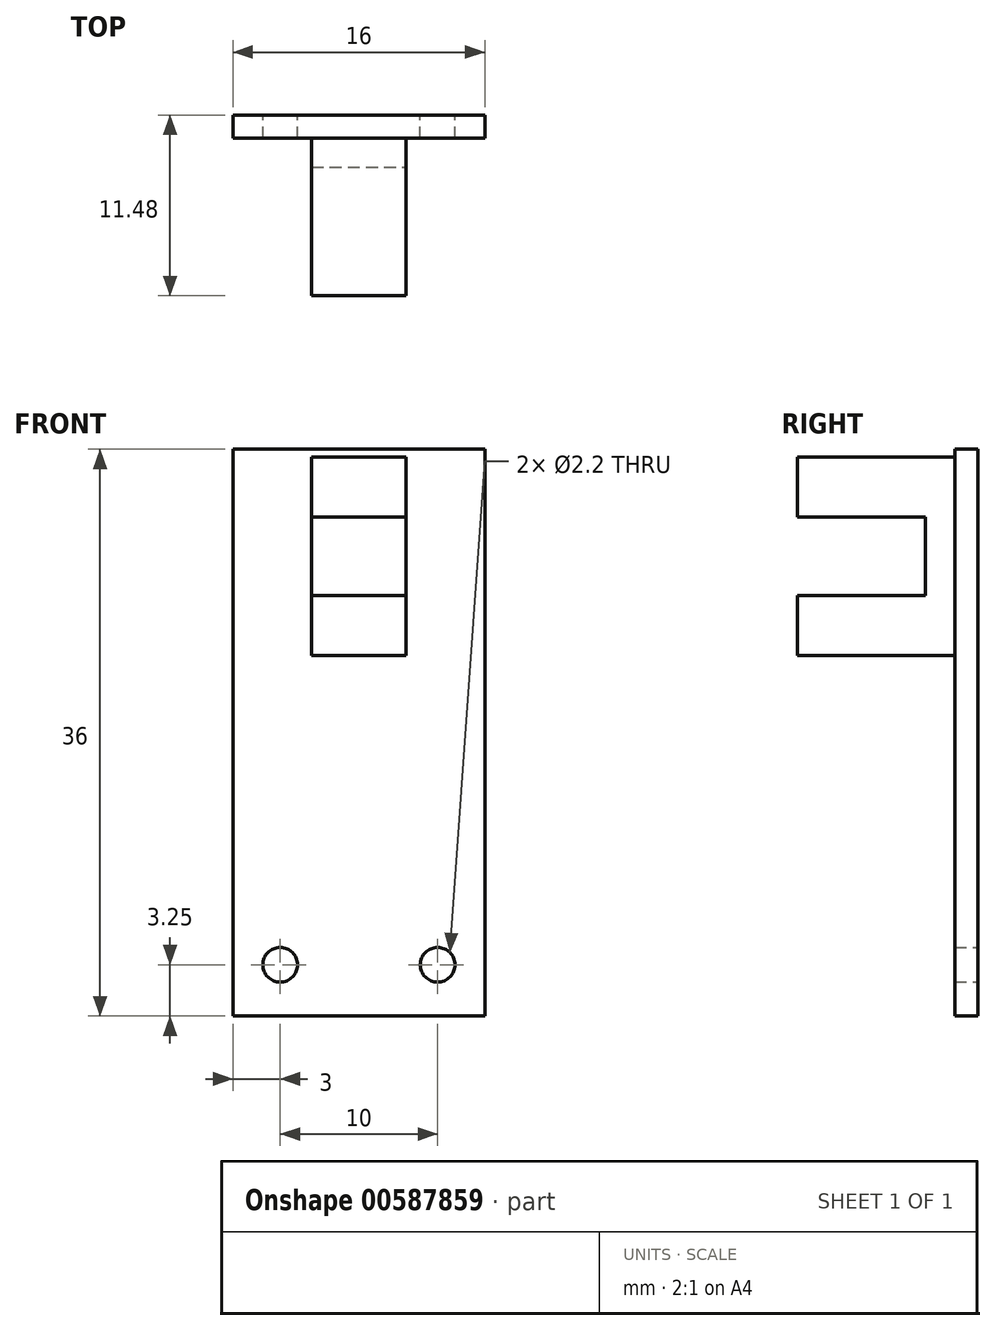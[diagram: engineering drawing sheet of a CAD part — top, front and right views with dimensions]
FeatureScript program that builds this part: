
annotation { "Feature Type Name" : "Feature", "Feature Type Description" : "" }
export const myFeature = defineFeature(function(context is Context, id is Id, definition is map)
    precondition{}
    {
        {
            var Q0;
            Q0=qCreatedBy(makeId("Front.planeOp"),FACE);
            var sketch = newSketch(context, id + "F0", { "sketchPlane" : qUnion([Q0])});
            skLineSegment(sketch, "E0.bottom", {"start": v(0, 0) * mm, "end": v(16, 0) * mm});
            skLineSegment(sketch, "E0.top", {"start": v(0, -36) * mm, "end": v(16, -36) * mm});
            skLineSegment(sketch, "E0.left", {"start": v(0, 0) * mm, "end": v(0, -36) * mm});
            skLineSegment(sketch, "E0.right", {"start": v(16, 0) * mm, "end": v(16, -36) * mm});
            skCircle(sketch, "E1", {"center": v(3, -32.75) * mm, "radius": 1.1 * mm});
            skCircle(sketch, "E2", {"center": v(13, -32.75) * mm, "radius": 1.1 * mm});
            skPoint(sketch, "E3", {"position": v(8, -36) * mm});
            skLineSegment(sketch, "E4", {"start": v(3, -32.75) * mm, "end": v(13, -32.75) * mm, "construction": true});
            skPoint(sketch, "E5", {"position": v(8, -32.75) * mm});
            skSolve(sketch);
        }
        {
            var Q0;
            Q0=makeQuery(id+"F0.imprint","IMPRINT",FACE,{"disambiguationData":[TD([[makeQuery(id+"F0.imprint","IMPRINT",EDGE,{"derivedFrom":sQuery(id+"F0.wireOp",EDGE,"E0.bottom")}),-1.0]])]});
            extrude(context, id + "F1", {"entities" : qUnion([Q0]), "depth" : 1.48 * mm, "offsetDistance" : 25 * mm});
        }
        {
            var Q0;
            Q0=makeQuery(id+"F1.opExtrude","CAP_FACE",FACE,{"disambiguationData":[OSD([sQuery(id+"F0.wireOp",EDGE,"E0.bottom"),sQuery(id+"F0.wireOp",EDGE,"E0.top"),sQuery(id+"F0.wireOp",EDGE,"E0.left"),sQuery(id+"F0.wireOp",EDGE,"E0.right")])],"isStart":false});
            var sketch = newSketch(context, id + "F2", { "sketchPlane" : qUnion([Q0])});
            skSolve(sketch);
        }
        {
            var Q0;
            Q0=makeQuery(id+"F2.imprint","IMPRINT",FACE,{"disambiguationData":[TD([[makeQuery(id+"F2.imprint","IMPRINT",EDGE,{"derivedFrom":makeQuery(id+"F1.opExtrude","CAP_EDGE",EDGE,{"disambiguationData":[OSD([sQuery(id+"F0.wireOp",EDGE,"E0.bottom")])],"isStart":false})}),-1.0]])]});
            var sketch = newSketch(context, id + "F3", { "sketchPlane" : qUnion([Q0])});
            skLineSegment(sketch, "E6.bottom", {"start": v(5, -0.5) * mm, "end": v(11, -0.5) * mm});
            skLineSegment(sketch, "E6.top", {"start": v(5, -13.1) * mm, "end": v(11, -13.1) * mm});
            skLineSegment(sketch, "E6.left", {"start": v(5, -0.5) * mm, "end": v(5, -13.1) * mm});
            skLineSegment(sketch, "E6.right", {"start": v(11, -0.5) * mm, "end": v(11, -13.1) * mm});
            skPoint(sketch, "E7", {"position": v(8, -0.5) * mm});
            skLineSegment(sketch, "E8.0", {"start": v(0, 0) * mm, "end": v(16, 0) * mm, "construction": true});
            skPoint(sketch, "E9", {"position": v(8, 0) * mm});
            skLineSegment(sketch, "E10", {"start": v(5, -4.3) * mm, "end": v(11, -4.3) * mm});
            skLineSegment(sketch, "E11", {"start": v(5, -9.3) * mm, "end": v(11, -9.3) * mm});
            skSolve(sketch);
        }
        {
            var Q0;
            {var subQ0=sQuery(id+"F3.wireOp",EDGE,"E6.top");Q0=makeQuery(id+"F3.imprint","IMPRINT",FACE,{"disambiguationData":[TD([[makeQuery(id+"F3.imprint","IMPRINT",EDGE,{"derivedFrom":subQ0}),1.0]])]});}
            var Q1;
            {var subQ0=sQuery(id+"F3.wireOp",EDGE,"E6.bottom");Q1=makeQuery(id+"F3.imprint","IMPRINT",FACE,{"disambiguationData":[TD([[makeQuery(id+"F3.imprint","IMPRINT",EDGE,{"derivedFrom":subQ0}),-1.0]])]});}
            extrude(context, id + "F4", {"entities" : qUnion([Q0, Q1]), "operationType" : NewBodyOperationType.ADD, "depth" : 10 * mm, "offsetDistance" : 25 * mm});
        }
        {
            var Q0;
            {var subQ0=sQuery(id+"F3.wireOp",EDGE,"E10");Q0=makeQuery(id+"F3.imprint","IMPRINT",FACE,{"disambiguationData":[TD([[makeQuery(id+"F3.imprint","IMPRINT",EDGE,{"derivedFrom":subQ0}),-1.0]])]});}
            extrude(context, id + "F5", {"entities" : qUnion([Q0]), "operationType" : NewBodyOperationType.ADD, "depth" : 1.85 * mm, "offsetDistance" : 25 * mm});
        }
    });
